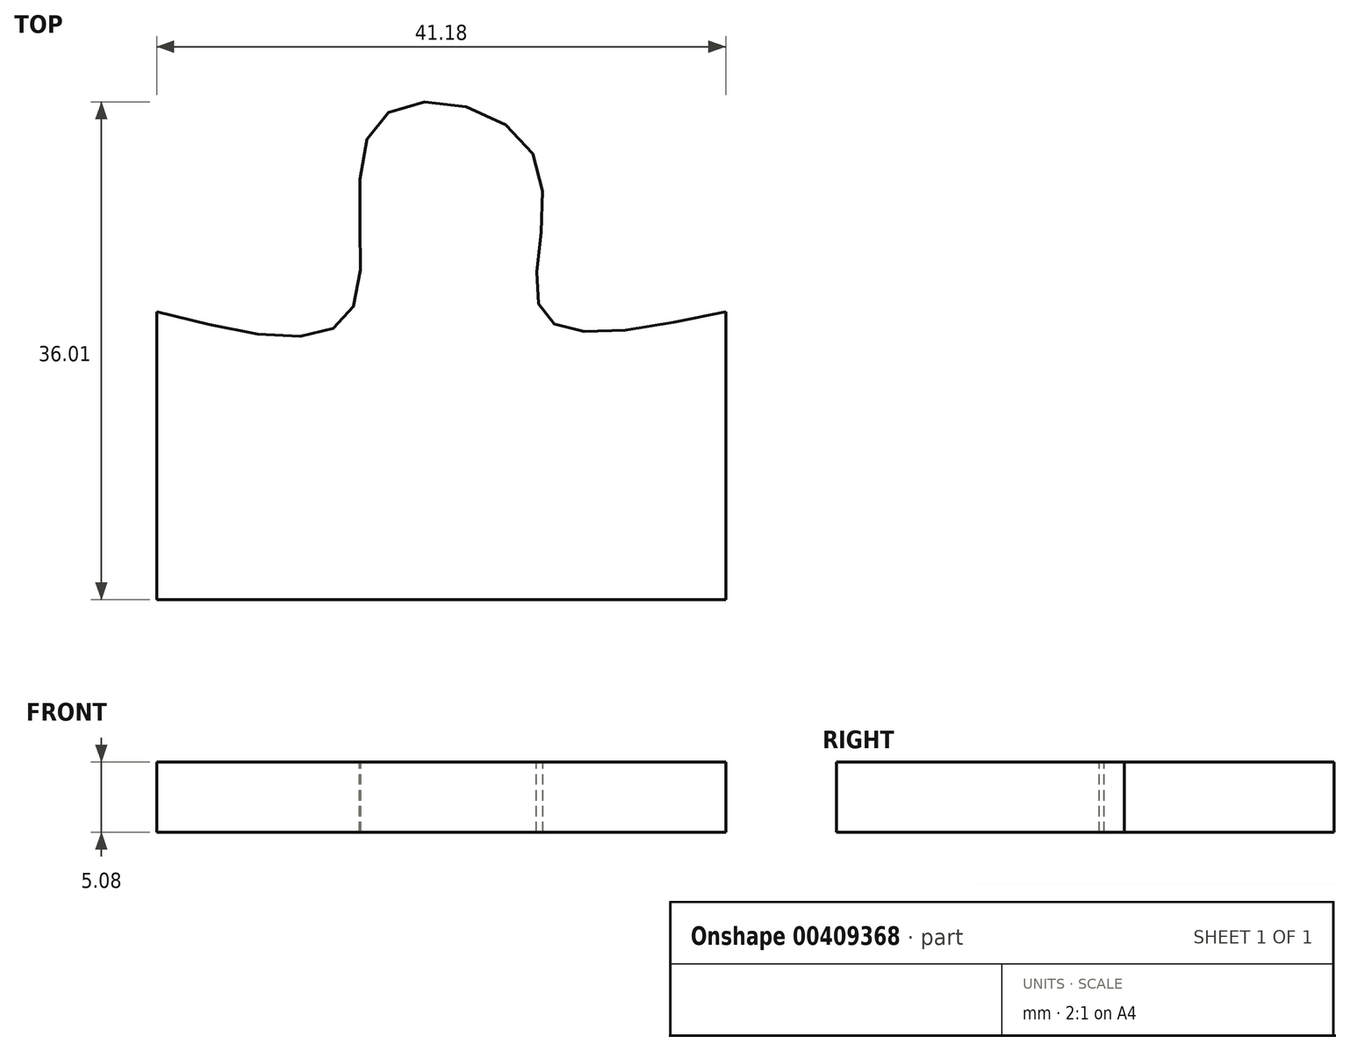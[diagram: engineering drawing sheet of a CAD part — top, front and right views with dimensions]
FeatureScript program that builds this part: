
annotation { "Feature Type Name" : "Feature", "Feature Type Description" : "" }
export const myFeature = defineFeature(function(context is Context, id is Id, definition is map)
    precondition{}
    {
        {
            var Q0;
            Q0=qCreatedBy(makeId("Top.planeOp"),FACE);
            var sketch = newSketch(context, id + "F0", { "sketchPlane" : qUnion([Q0])});
            skLineSegment(sketch, "E0", {"start": v(0, 0) * mm, "end": v(41.18, 0) * mm});
            skLineSegment(sketch, "E1", {"start": v(41.18, 0) * mm, "end": v(41.18, 20.83) * mm});
            skFitSpline(sketch, "E2", {"points": [v(41.18, 20.83) * mm, v(27.86, 20.83) * mm, v(27.12, 32.42) * mm, v(16.03, 34.64) * mm, v(14.05, 20.83) * mm, v(0, 20.83) * mm], "startDerivative": vector(-87.62, -18.7) * mm, "endDerivative": vector(-87.8, 22.45) * mm});
            skLineSegment(sketch, "E3", {"start": v(0, 20.83) * mm, "end": v(0, 0) * mm});
            skSolve(sketch);
        }
        {
            var Q0;
            Q0=makeQuery(id+"F0.imprint","IMPRINT",FACE,{"disambiguationData":[TD([[makeQuery(id+"F0.imprint","IMPRINT",EDGE,{"derivedFrom":sQuery(id+"F0.wireOp",EDGE,"E0")}),1.0]])]});
            extrude(context, id + "F1", {"entities" : qUnion([Q0]), "depth" : 25.4 * mm});
        }
        {
            var Q0;
            Q0=makeQuery(id+"F1.opExtrude","CAP_FACE",FACE,{"disambiguationData":[OSD([sQuery(id+"F0.wireOp",EDGE,"E0"),sQuery(id+"F0.wireOp",EDGE,"E1"),sQuery(id+"F0.wireOp",EDGE,"E2"),sQuery(id+"F0.wireOp",EDGE,"E3")])],"isStart":false});
            extrude(context, id + "F2", {"entities" : qUnion([Q0]), "operationType" : NewBodyOperationType.REMOVE, "oppositeDirection" : true, "depth" : 20.32 * mm});
        }
    });
